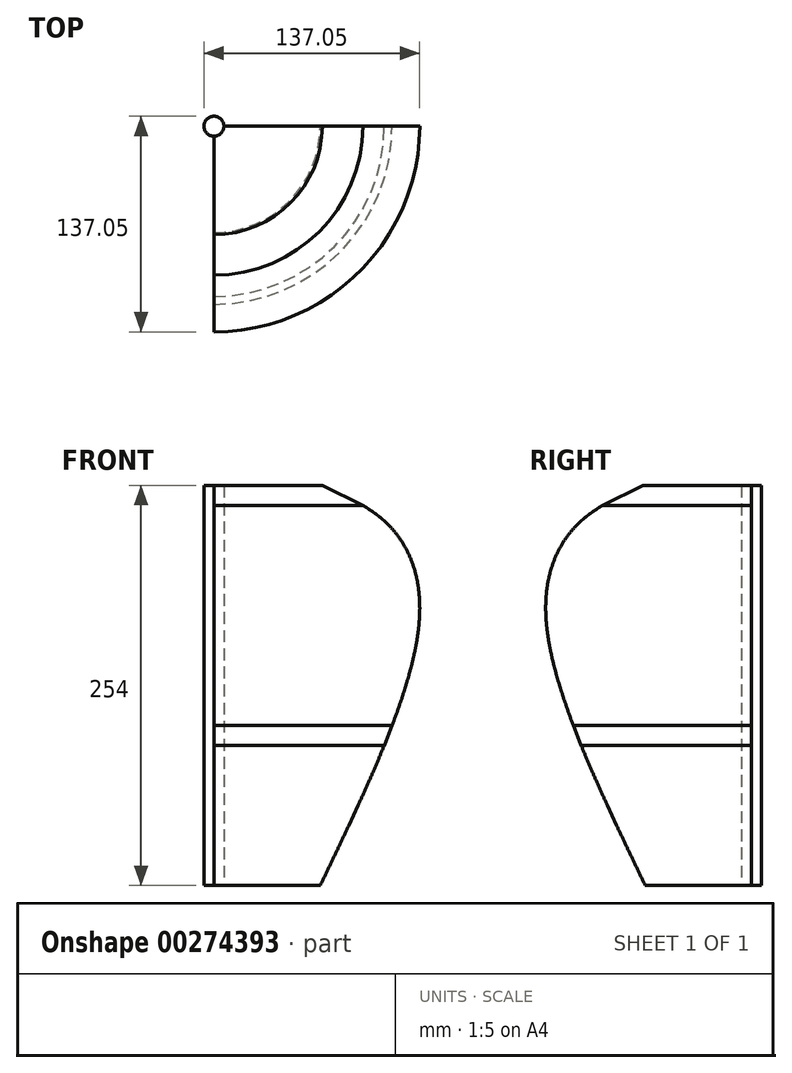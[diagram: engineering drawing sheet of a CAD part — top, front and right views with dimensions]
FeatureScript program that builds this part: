
annotation { "Feature Type Name" : "Feature", "Feature Type Description" : "" }
export const myFeature = defineFeature(function(context is Context, id is Id, definition is map)
    precondition{}
    {
        {
            var Q0;
            Q0=qCreatedBy(makeId("Top.planeOp"),FACE);
            var sketch = newSketch(context, id + "F0", { "sketchPlane" : qUnion([Q0])});
            skCircle(sketch, "E0", {"center": v(0, 0) * mm, "radius": 6.35 * mm});
            skSolve(sketch);
        }
        {
            var Q0;
            Q0=makeQuery(id+"F0.imprint","IMPRINT",FACE,{"disambiguationData":[TD([[makeQuery(id+"F0.imprint","IMPRINT",EDGE,{"derivedFrom":sQuery(id+"F0.wireOp",EDGE,"E0")}),1.0]])]});
            extrude(context, id + "F1", {"entities" : qUnion([Q0]), "endBound" : BoundingType.SYMMETRIC, "depth" : 254 * mm});
        }
        {
            var Q0;
            Q0=qCreatedBy(makeId("Front.planeOp"),FACE);
            var sketch = newSketch(context, id + "F2", { "sketchPlane" : qUnion([Q0])});
            skLineSegment(sketch, "E1", {"start": v(6.35, 127) * mm, "end": v(6.35, -127) * mm});
            skLineSegment(sketch, "E2", {"start": v(6.35, 127) * mm, "end": v(68.84, 127) * mm});
            skLineSegment(sketch, "E3", {"start": v(6.35, -127) * mm, "end": v(67.53, -127) * mm});
            skFitSpline(sketch, "E4", {"points": [v(68.84, 127) * mm, v(111.6, 101.13) * mm, v(130.5, 42.47) * mm, v(67.53, -127) * mm], "startDerivative": vector(188.08, -83.57) * mm, "endDerivative": vector(-190.53, -396.37) * mm});
            skLineSegment(sketch, "E5.0.1.0", {"start": v(170.44, 88.9) * mm, "end": v(120.81, 88.9) * mm});
            skLineSegment(sketch, "E5.0.1.2", {"start": v(111.14, 101.6) * mm, "end": v(170.44, 101.6) * mm});
            skLineSegment(sketch, "E5.0.2.0", {"start": v(170.44, 63.5) * mm, "end": v(129.62, 63.5) * mm});
            skLineSegment(sketch, "E5.0.2.1", {"start": v(170.44, 76.2) * mm, "end": v(170.44, 63.5) * mm});
            skLineSegment(sketch, "E5.0.2.2", {"start": v(126.54, 76.2) * mm, "end": v(170.44, 76.2) * mm});
            skLineSegment(sketch, "E5.0.3.0", {"start": v(170.44, 38.1) * mm, "end": v(130.14, 38.1) * mm});
            skLineSegment(sketch, "E5.0.3.1", {"start": v(170.44, 50.8) * mm, "end": v(170.44, 38.1) * mm});
            skLineSegment(sketch, "E5.0.3.2", {"start": v(130.69, 50.8) * mm, "end": v(170.44, 50.8) * mm});
            skLineSegment(sketch, "E5.0.4.0", {"start": v(170.44, 12.7) * mm, "end": v(125.48, 12.7) * mm});
            skLineSegment(sketch, "E5.0.4.1", {"start": v(170.44, 25.4) * mm, "end": v(170.44, 12.7) * mm});
            skLineSegment(sketch, "E5.0.4.2", {"start": v(128.3, 25.4) * mm, "end": v(170.44, 25.4) * mm});
            skLineSegment(sketch, "E5.0.5.0", {"start": v(170.44, -12.7) * mm, "end": v(117.77, -12.7) * mm});
            skLineSegment(sketch, "E5.0.5.1", {"start": v(170.44, 0) * mm, "end": v(170.44, -12.7) * mm});
            skLineSegment(sketch, "E5.0.5.2", {"start": v(121.92, 0) * mm, "end": v(170.44, 0) * mm});
            skLineSegment(sketch, "E5.0.7.0", {"start": v(170.44, -63.5) * mm, "end": v(97.31, -63.5) * mm});
            skLineSegment(sketch, "E5.0.7.2", {"start": v(102.86, -50.8) * mm, "end": v(170.44, -50.8) * mm});
            skLineSegment(sketch, "E5.0.9.0", {"start": v(170.44, -114.3) * mm, "end": v(73.63, -114.3) * mm});
            skLineSegment(sketch, "E5.0.9.1", {"start": v(170.44, -101.6) * mm, "end": v(170.44, -114.3) * mm});
            skLineSegment(sketch, "E5.0.9.2", {"start": v(79.7, -101.6) * mm, "end": v(170.44, -101.6) * mm});
            skLineSegment(sketch, "E6", {"start": v(0, 160.15) * mm, "end": v(0, -169.37) * mm, "construction": true});
            skLineSegment(sketch, "E7", {"start": v(85.69, -88.9) * mm, "end": v(91.57, -76.2) * mm});
            skLineSegment(sketch, "E8", {"start": v(108.16, -38.1) * mm, "end": v(113.16, -25.4) * mm});
            skLineSegment(sketch, "E9", {"start": v(94.62, 114.3) * mm, "end": v(68.84, 127) * mm});
            skLineSegment(sketch, "E10", {"start": v(170.44, 101.6) * mm, "end": v(229.34, 101.6) * mm});
            skLineSegment(sketch, "E11", {"start": v(229.34, 101.6) * mm, "end": v(229.34, 88.9) * mm});
            skLineSegment(sketch, "E12", {"start": v(229.34, 88.9) * mm, "end": v(170.44, 88.9) * mm});
            skLineSegment(sketch, "E13", {"start": v(170.44, -50.8) * mm, "end": v(229.34, -50.8) * mm});
            skLineSegment(sketch, "E14", {"start": v(229.34, -50.8) * mm, "end": v(229.34, -63.5) * mm});
            skLineSegment(sketch, "E15", {"start": v(229.34, -63.5) * mm, "end": v(170.44, -63.5) * mm});
            skSolve(sketch);
        }
        {
            var Q0;
            Q0=makeQuery(id+"F2.imprint","IMPRINT",FACE,{"disambiguationData":[TD([[makeQuery(id+"F2.imprint","IMPRINT",EDGE,{"derivedFrom":sQuery(id+"F2.wireOp",EDGE,"E1")}),1.0]])]});
            var Q1;
            Q1=sQuery(id+"F2.wireOp",EDGE,"E6");
            revolve(context, id + "F3", {"entities" : qUnion([Q0]), "axis" : qUnion([Q1]), "revolveType" : RevolveType.ONE_DIRECTION, "angle" : 90 * degree});
        }
    });
